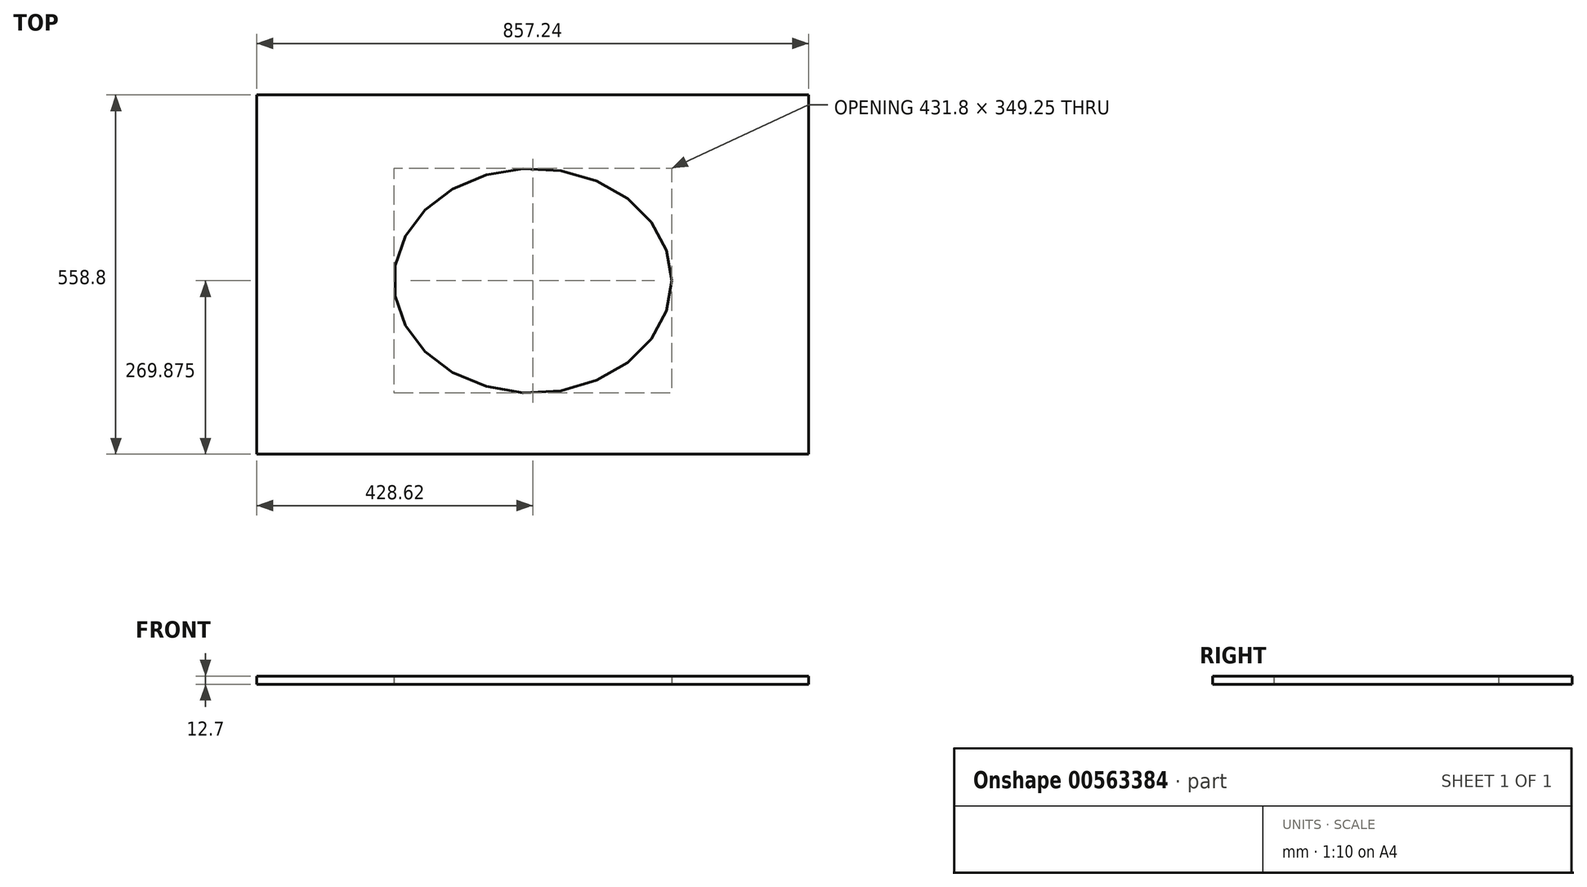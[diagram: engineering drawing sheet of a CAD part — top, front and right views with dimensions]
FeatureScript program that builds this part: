
annotation { "Feature Type Name" : "Feature", "Feature Type Description" : "" }
export const myFeature = defineFeature(function(context is Context, id is Id, definition is map)
    precondition{}
    {
        {
            var Q0;
            Q0=qCreatedBy(makeId("Top.planeOp"),FACE);
            var sketch = newSketch(context, id + "F0", { "sketchPlane" : qUnion([Q0])});
            skLineSegment(sketch, "E0.bottom", {"start": v(-428.62, 279.4) * mm, "end": v(428.63, 279.4) * mm});
            skLineSegment(sketch, "E0.top", {"start": v(-428.63, -279.4) * mm, "end": v(428.62, -279.4) * mm});
            skLineSegment(sketch, "E0.left", {"start": v(-428.62, 279.4) * mm, "end": v(-428.63, -279.4) * mm});
            skLineSegment(sketch, "E0.right", {"start": v(428.63, 279.4) * mm, "end": v(428.62, -279.4) * mm});
            skLineSegment(sketch, "E1", {"start": v(-428.62, 279.4) * mm, "end": v(428.62, -279.4) * mm, "construction": true});
            skLineSegment(sketch, "E2", {"start": v(-428.63, -279.4) * mm, "end": v(428.62, 279.4) * mm, "construction": true});
            skLineSegment(sketch, "E3", {"start": v(-428.63, -184.15) * mm, "end": v(428.63, -184.15) * mm, "construction": true});
            skLineSegment(sketch, "E4", {"start": v(-428.62, 165.1) * mm, "end": v(428.63, 165.1) * mm, "construction": true});
            skLineSegment(sketch, "E5", {"start": v(215.9, 165.1) * mm, "end": v(215.9, -184.15) * mm, "construction": true});
            skLineSegment(sketch, "E6", {"start": v(-215.9, 165.1) * mm, "end": v(-215.9, -184.15) * mm, "construction": true});
            skEllipse(sketch, "E7", {"center": v(0, -9.53) * mm, "majorRadius": 215.9 * mm, "minorRadius": 174.63 * mm, "majorAxis": v(1, 0)});
            skSolve(sketch);
        }
        {
            var Q0;
            Q0=makeQuery(id+"F0.imprint","IMPRINT",FACE,{"disambiguationData":[TD([[makeQuery(id+"F0.imprint","IMPRINT",EDGE,{"derivedFrom":sQuery(id+"F0.wireOp",EDGE,"E0.bottom")}),-1.0]])]});
            extrude(context, id + "F1", {"entities" : qUnion([Q0]), "depth" : 12.7 * mm, "offsetDistance" : 25.4 * mm});
        }
    });
